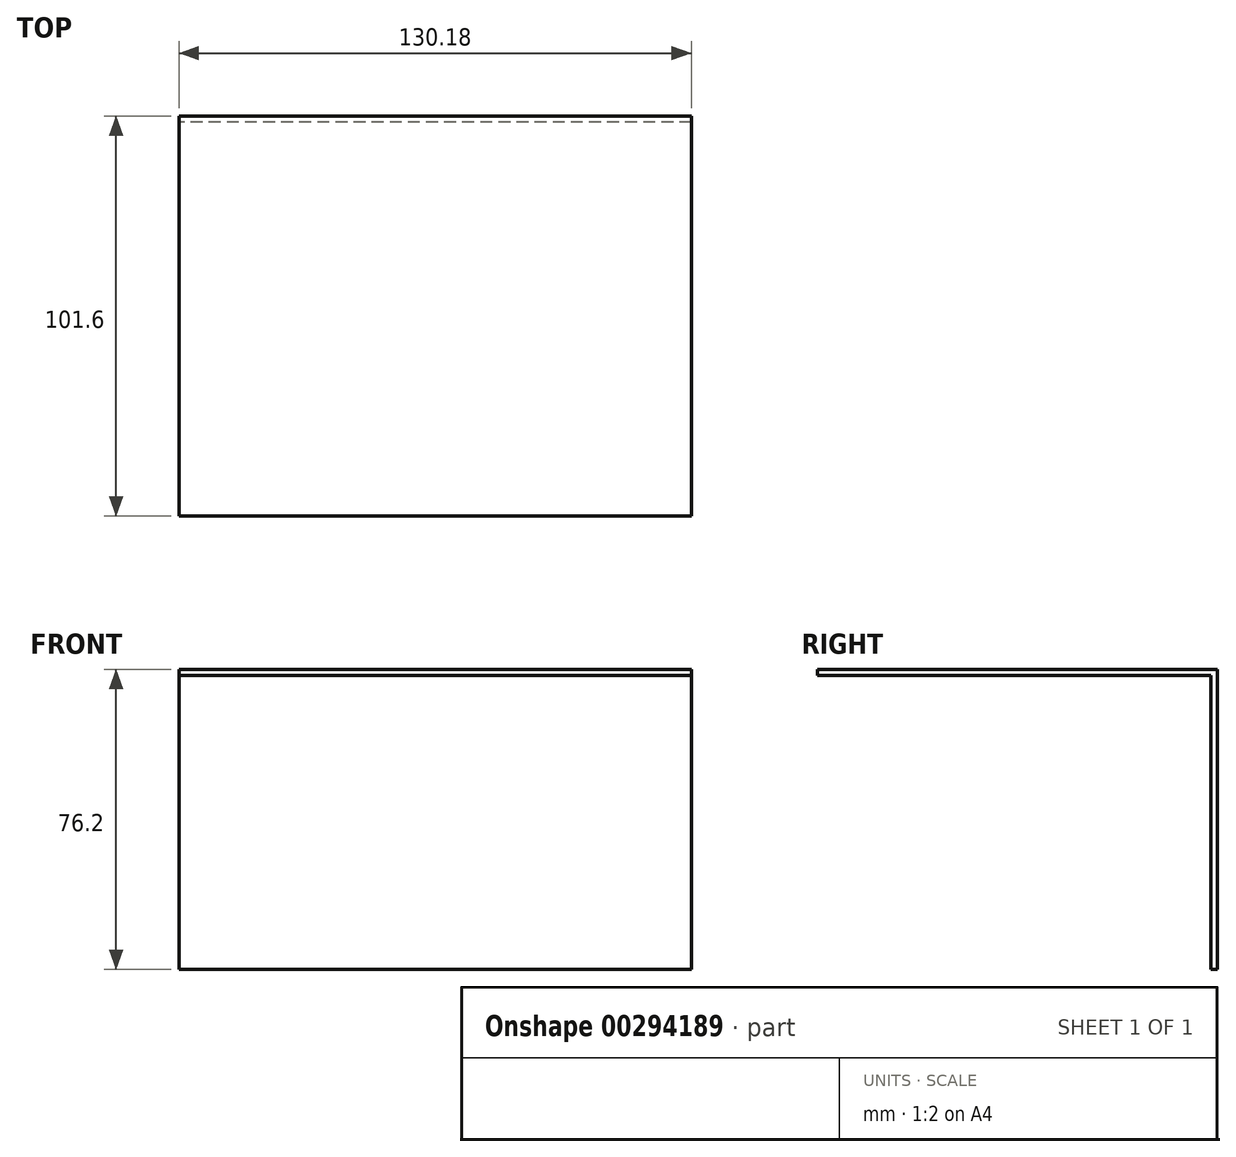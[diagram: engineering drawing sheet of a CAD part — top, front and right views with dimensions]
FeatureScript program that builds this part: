
annotation { "Feature Type Name" : "Feature", "Feature Type Description" : "" }
export const myFeature = defineFeature(function(context is Context, id is Id, definition is map)
    precondition{}
    {
        {
            var Q0;
            Q0=qCreatedBy(makeId("Right.planeOp"),FACE);
            var sketch = newSketch(context, id + "F0", { "sketchPlane" : qUnion([Q0])});
            skLineSegment(sketch, "E0", {"start": v(16.15, -1.18) * mm, "end": v(16.15, 0.4) * mm});
            skLineSegment(sketch, "E1", {"start": v(16.15, 0.4) * mm, "end": v(117.75, 0.4) * mm});
            skLineSegment(sketch, "E2", {"start": v(117.75, 0.4) * mm, "end": v(117.75, -75.8) * mm});
            skLineSegment(sketch, "E3", {"start": v(117.75, -75.8) * mm, "end": v(116.18, -75.8) * mm});
            skLineSegment(sketch, "E4", {"start": v(116.18, -75.8) * mm, "end": v(116.18, -1.18) * mm});
            skLineSegment(sketch, "E5", {"start": v(116.18, -1.18) * mm, "end": v(16.15, -1.18) * mm});
            skSolve(sketch);
        }
        {
            var Q0;
            Q0=makeQuery(id+"F0.imprint","IMPRINT",FACE,{"disambiguationData":[TD([[makeQuery(id+"F0.imprint","IMPRINT",EDGE,{"derivedFrom":sQuery(id+"F0.wireOp",EDGE,"E0")}),-1.0]])]});
            extrude(context, id + "F1", {"entities" : qUnion([Q0]), "depth" : 130.17 * mm});
        }
    });
